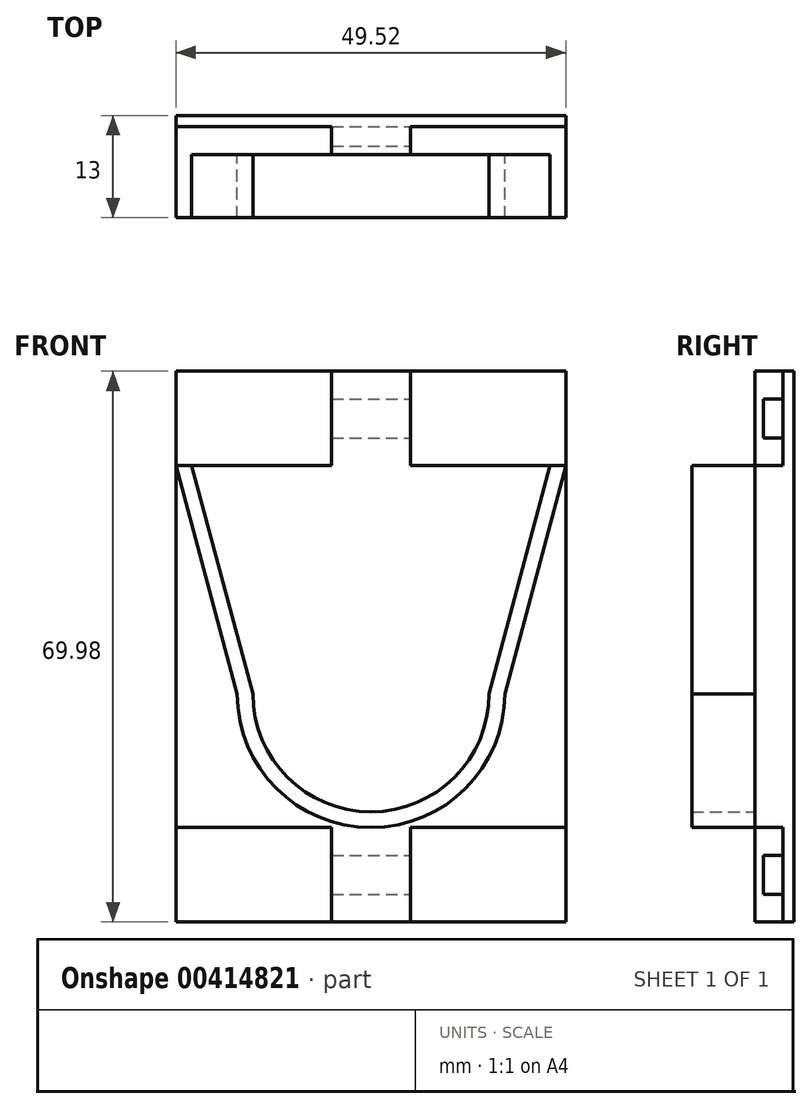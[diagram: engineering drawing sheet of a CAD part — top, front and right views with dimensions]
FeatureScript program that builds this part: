
annotation { "Feature Type Name" : "Feature", "Feature Type Description" : "" }
export const myFeature = defineFeature(function(context is Context, id is Id, definition is map)
    precondition{}
    {
        {
            var Q0;
            Q0=qCreatedBy(makeId("Front.planeOp"),FACE);
            var sketch = newSketch(context, id + "F0", { "sketchPlane" : qUnion([Q0])});
            skArc(sketch, "E0", {"start": v(-15, 0) * mm, "mid": v(0, -15) * mm, "end": v(15, 0) * mm});
            skLineSegment(sketch, "E1", {"start": v(15, 0) * mm, "end": v(22.76, 28.98) * mm});
            skLineSegment(sketch, "E2.MirrorCS", {"start": v(-15, 0) * mm, "end": v(-22.76, 28.98) * mm});
            skArc(sketch, "E3", {"start": v(-17, 0) * mm, "mid": v(0, -17) * mm, "end": v(17, 0) * mm});
            skLineSegment(sketch, "E4", {"start": v(-22.76, 28.98) * mm, "end": v(-24.76, 28.98) * mm});
            skLineSegment(sketch, "E5", {"start": v(-24.76, 28.98) * mm, "end": v(-17, 0) * mm});
            skLineSegment(sketch, "E6", {"start": v(22.76, 28.98) * mm, "end": v(24.76, 28.98) * mm});
            skLineSegment(sketch, "E7", {"start": v(24.76, 28.98) * mm, "end": v(17, 0) * mm});
            skSolve(sketch);
        }
        {
            var Q0;
            Q0 = qSketchRegion(id + "F0", true);
            extrude(context, id + "F1", {"entities" : qUnion([Q0]), "depth" : 8 * mm});
        }
        {
            var Q0;
            Q0=qCreatedBy(makeId("Front.planeOp"),FACE);
            var sketch = newSketch(context, id + "F2", { "sketchPlane" : qUnion([Q0])});
            skLineSegment(sketch, "E8.bottom", {"start": v(24.76, 28.98) * mm, "end": v(-24.76, 28.98) * mm});
            skLineSegment(sketch, "E8.top", {"start": v(24.76, -17) * mm, "end": v(-24.76, -17) * mm});
            skLineSegment(sketch, "E8.left", {"start": v(24.76, 28.98) * mm, "end": v(24.76, -17) * mm});
            skLineSegment(sketch, "E8.right", {"start": v(-24.76, 28.98) * mm, "end": v(-24.76, -17) * mm});
            skSolve(sketch);
        }
        {
            var Q0;
            Q0 = qSketchRegion(id + "F2", true);
            extrude(context, id + "F3", {"entities" : qUnion([Q0]), "operationType" : NewBodyOperationType.ADD, "oppositeDirection" : true, "depth" : 5 * mm});
        }
        {
            var Q0;
            Q0=makeQuery(id+"F3.opExtrude","SWEPT_FACE",FACE,{"disambiguationData":[OSD([sQuery(id+"F2.wireOp",EDGE,"E8.top")])]});
            var sketch = newSketch(context, id + "F4", { "sketchPlane" : qUnion([Q0])});
            skLineSegment(sketch, "E9", {"start": v(-5, 0) * mm, "end": v(5, 0) * mm});
            skLineSegment(sketch, "E10", {"start": v(-5, 0) * mm, "end": v(-5, -3.6) * mm});
            skLineSegment(sketch, "E11", {"start": v(-5, -3.6) * mm, "end": v(-24.76, -3.6) * mm});
            skLineSegment(sketch, "E12", {"start": v(-24.76, -3.6) * mm, "end": v(-24.76, -5) * mm});
            skLineSegment(sketch, "E13", {"start": v(-24.76, -5) * mm, "end": v(24.76, -5) * mm});
            skLineSegment(sketch, "E14", {"start": v(24.76, -5) * mm, "end": v(24.76, -3.6) * mm});
            skLineSegment(sketch, "E15", {"start": v(24.76, -3.6) * mm, "end": v(5, -3.6) * mm});
            skLineSegment(sketch, "E16", {"start": v(5, -3.6) * mm, "end": v(5, 0) * mm});
            skSolve(sketch);
        }
        {
            var Q0;
            Q0 = qSketchRegion(id + "F4", true);
            extrude(context, id + "F5", {"entities" : qUnion([Q0]), "operationType" : NewBodyOperationType.ADD, "depth" : 12 * mm});
        }
        {
            var Q0;
            Q0=makeQuery(id+"F5.opExtrude","SWEPT_FACE",FACE,{"disambiguationData":[OSD([sQuery(id+"F4.wireOp",EDGE,"E16")])]});
            var sketch = newSketch(context, id + "F6", { "sketchPlane" : qUnion([Q0])});
            skLineSegment(sketch, "E17.bottom", {"start": v(1.1, -25.5) * mm, "end": v(3.6, -25.5) * mm});
            skLineSegment(sketch, "E17.top", {"start": v(1.1, -20.5) * mm, "end": v(3.6, -20.5) * mm});
            skLineSegment(sketch, "E17.left", {"start": v(1.1, -25.5) * mm, "end": v(1.1, -20.5) * mm});
            skLineSegment(sketch, "E17.right", {"start": v(3.6, -25.5) * mm, "end": v(3.6, -20.5) * mm});
            skSolve(sketch);
        }
        {
            var Q0;
            Q0 = qSketchRegion(id + "F6", true);
            extrude(context, id + "F7", {"entities" : qUnion([Q0]), "operationType" : NewBodyOperationType.REMOVE, "endBound" : BoundingType.THROUGH_ALL, "oppositeDirection" : true, "depth" : 25 * mm});
        }
        {
            var Q0;
            Q0=makeQuery(id+"F3.boolean.opBoolean","MERGE",FACE,{"derivedFrom":[makeQuery(id+"F1.opExtrude","SWEPT_FACE",FACE,{"disambiguationData":[OSD([sQuery(id+"F0.wireOp",EDGE,"E4")])]}),makeQuery(id+"F1.opExtrude","SWEPT_FACE",FACE,{"disambiguationData":[OSD([sQuery(id+"F0.wireOp",EDGE,"E6")])]}),makeQuery(id+"F3.opExtrude","SWEPT_FACE",FACE,{"disambiguationData":[OSD([sQuery(id+"F2.wireOp",EDGE,"E8.bottom")])]})]});
            var sketch = newSketch(context, id + "F8", { "sketchPlane" : qUnion([Q0])});
            skLineSegment(sketch, "E18", {"start": v(-24.76, 5) * mm, "end": v(24.76, 5) * mm});
            skLineSegment(sketch, "E19.MirrorCS", {"start": v(-5, 0) * mm, "end": v(5, 0) * mm});
            skLineSegment(sketch, "E20.MirrorCS", {"start": v(5, 3.6) * mm, "end": v(5, 0) * mm});
            skLineSegment(sketch, "E21.MirrorCS", {"start": v(-5, 0) * mm, "end": v(-5, 3.6) * mm});
            skLineSegment(sketch, "E22.MirrorCS", {"start": v(-5, 3.6) * mm, "end": v(-24.76, 3.6) * mm});
            skLineSegment(sketch, "E23.MirrorCS", {"start": v(24.76, 3.6) * mm, "end": v(5, 3.6) * mm});
            skLineSegment(sketch, "E24.MirrorCS", {"start": v(24.76, 5) * mm, "end": v(24.76, 3.6) * mm});
            skLineSegment(sketch, "E25.MirrorCS", {"start": v(-24.76, 3.6) * mm, "end": v(-24.76, 5) * mm});
            skSolve(sketch);
        }
        {
            var Q0;
            Q0 = qSketchRegion(id + "F8", true);
            extrude(context, id + "F9", {"entities" : qUnion([Q0]), "operationType" : NewBodyOperationType.ADD, "depth" : 12 * mm});
        }
        {
            var Q0;
            Q0=makeQuery(id+"F9.opExtrude","SWEPT_FACE",FACE,{"disambiguationData":[OSD([sQuery(id+"F8.wireOp",EDGE,"E20.MirrorCS")])]});
            var sketch = newSketch(context, id + "F10", { "sketchPlane" : qUnion([Q0])});
            skLineSegment(sketch, "E26.bottom", {"start": v(1.1, 37.48) * mm, "end": v(3.6, 37.48) * mm});
            skLineSegment(sketch, "E26.top", {"start": v(1.1, 32.48) * mm, "end": v(3.6, 32.48) * mm});
            skLineSegment(sketch, "E26.left", {"start": v(1.1, 37.48) * mm, "end": v(1.1, 32.48) * mm});
            skLineSegment(sketch, "E26.right", {"start": v(3.6, 37.48) * mm, "end": v(3.6, 32.48) * mm});
            skSolve(sketch);
        }
        {
            var Q0;
            Q0 = qSketchRegion(id + "F10", true);
            extrude(context, id + "F11", {"entities" : qUnion([Q0]), "operationType" : NewBodyOperationType.REMOVE, "endBound" : BoundingType.THROUGH_ALL, "oppositeDirection" : true, "depth" : 25 * mm});
        }
    });
